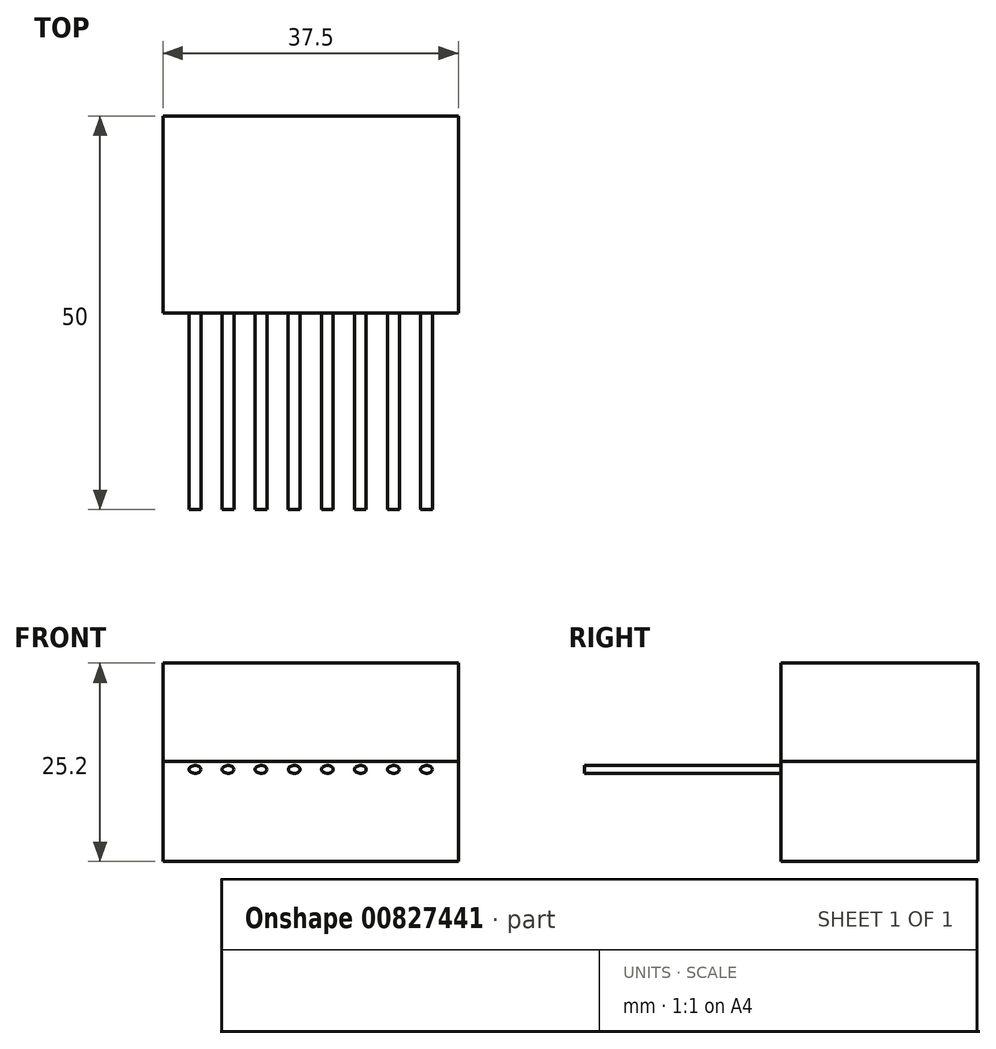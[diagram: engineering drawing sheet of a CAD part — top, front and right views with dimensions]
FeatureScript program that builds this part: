
annotation { "Feature Type Name" : "Feature", "Feature Type Description" : "" }
export const myFeature = defineFeature(function(context is Context, id is Id, definition is map)
    precondition{}
    {
        {
            var Q0;
            Q0=qCreatedBy(makeId("Front.planeOp"),FACE);
            var sketch = newSketch(context, id + "F0", { "sketchPlane" : qUnion([Q0])});
            skLineSegment(sketch, "E0.bottom", {"start": v(18.75, 6.35) * mm, "end": v(-18.75, 6.35) * mm});
            skLineSegment(sketch, "E0.top", {"start": v(18.75, -6.35) * mm, "end": v(-18.75, -6.35) * mm});
            skLineSegment(sketch, "E0.left", {"start": v(18.75, 6.35) * mm, "end": v(18.75, -6.35) * mm});
            skLineSegment(sketch, "E0.right", {"start": v(-18.75, 6.35) * mm, "end": v(-18.75, -6.35) * mm});
            skPoint(sketch, "E0.middle", {"position": v(0, 0) * mm});
            skSolve(sketch);
        }
        {
            var Q0;
            Q0=makeQuery(id+"F0.imprint","IMPRINT",FACE,{"disambiguationData":[TD([[makeQuery(id+"F0.imprint","IMPRINT",EDGE,{"derivedFrom":sQuery(id+"F0.wireOp",EDGE,"E0.bottom")}),1.0]])]});
            extrude(context, id + "F1", {"entities" : qUnion([Q0]), "depth" : 25 * mm, "offsetDistance" : 25 * mm});
        }
        {
            var Q0;
            Q0=makeQuery(id+"F1.opExtrude","CAP_FACE",FACE,{"disambiguationData":[OSD([sQuery(id+"F0.wireOp",EDGE,"E0.bottom"),sQuery(id+"F0.wireOp",EDGE,"E0.top"),sQuery(id+"F0.wireOp",EDGE,"E0.left"),sQuery(id+"F0.wireOp",EDGE,"E0.right")])],"isStart":false});
            var sketch = newSketch(context, id + "F2", { "sketchPlane" : qUnion([Q0])});
            skEllipse(sketch, "E1", {"center": v(-14.7, 5.35) * mm, "majorRadius": 0.75 * mm, "minorRadius": 0.5 * mm, "majorAxis": v(1, 0)});
            skEllipse(sketch, "E2.1.0.0", {"center": v(-10.5, 5.35) * mm, "majorRadius": 0.75 * mm, "minorRadius": 0.5 * mm, "majorAxis": v(1, 0)});
            skEllipse(sketch, "E2.2.0.0", {"center": v(-6.3, 5.35) * mm, "majorRadius": 0.75 * mm, "minorRadius": 0.5 * mm, "majorAxis": v(1, 0)});
            skEllipse(sketch, "E2.3.0.0", {"center": v(-2.1, 5.35) * mm, "majorRadius": 0.75 * mm, "minorRadius": 0.5 * mm, "majorAxis": v(1, 0)});
            skEllipse(sketch, "E2.4.0.0", {"center": v(2.1, 5.35) * mm, "majorRadius": 0.75 * mm, "minorRadius": 0.5 * mm, "majorAxis": v(1, 0)});
            skEllipse(sketch, "E2.5.0.0", {"center": v(6.3, 5.35) * mm, "majorRadius": 0.75 * mm, "minorRadius": 0.5 * mm, "majorAxis": v(1, 0)});
            skEllipse(sketch, "E2.6.0.0", {"center": v(10.5, 5.35) * mm, "majorRadius": 0.75 * mm, "minorRadius": 0.5 * mm, "majorAxis": v(1, 0)});
            skEllipse(sketch, "E2.7.0.0", {"center": v(14.7, 5.35) * mm, "majorRadius": 0.75 * mm, "minorRadius": 0.5 * mm, "majorAxis": v(1, 0)});
            skLineSegment(sketch, "E2.direction1", {"start": v(-14.7, 5.35) * mm, "end": v(-10.5, 5.35) * mm, "construction": true});
            skSolve(sketch);
        }
        {
            var Q0;
            Q0 = qSketchRegion(id + "F2", true);
            extrude(context, id + "F3", {"entities" : qUnion([Q0]), "depth" : 25 * mm, "offsetDistance" : 25 * mm});
        }
        {
            var Q0;
            Q0=makeQuery(id+"F1.opExtrude","SWEPT_FACE",FACE,{"disambiguationData":[OSD([sQuery(id+"F0.wireOp",EDGE,"E0.bottom")])]});
            extrude(context, id + "F4", {"entities" : qUnion([Q0]), "depth" : 12.5 * mm, "offsetDistance" : 25 * mm});
        }
    });
